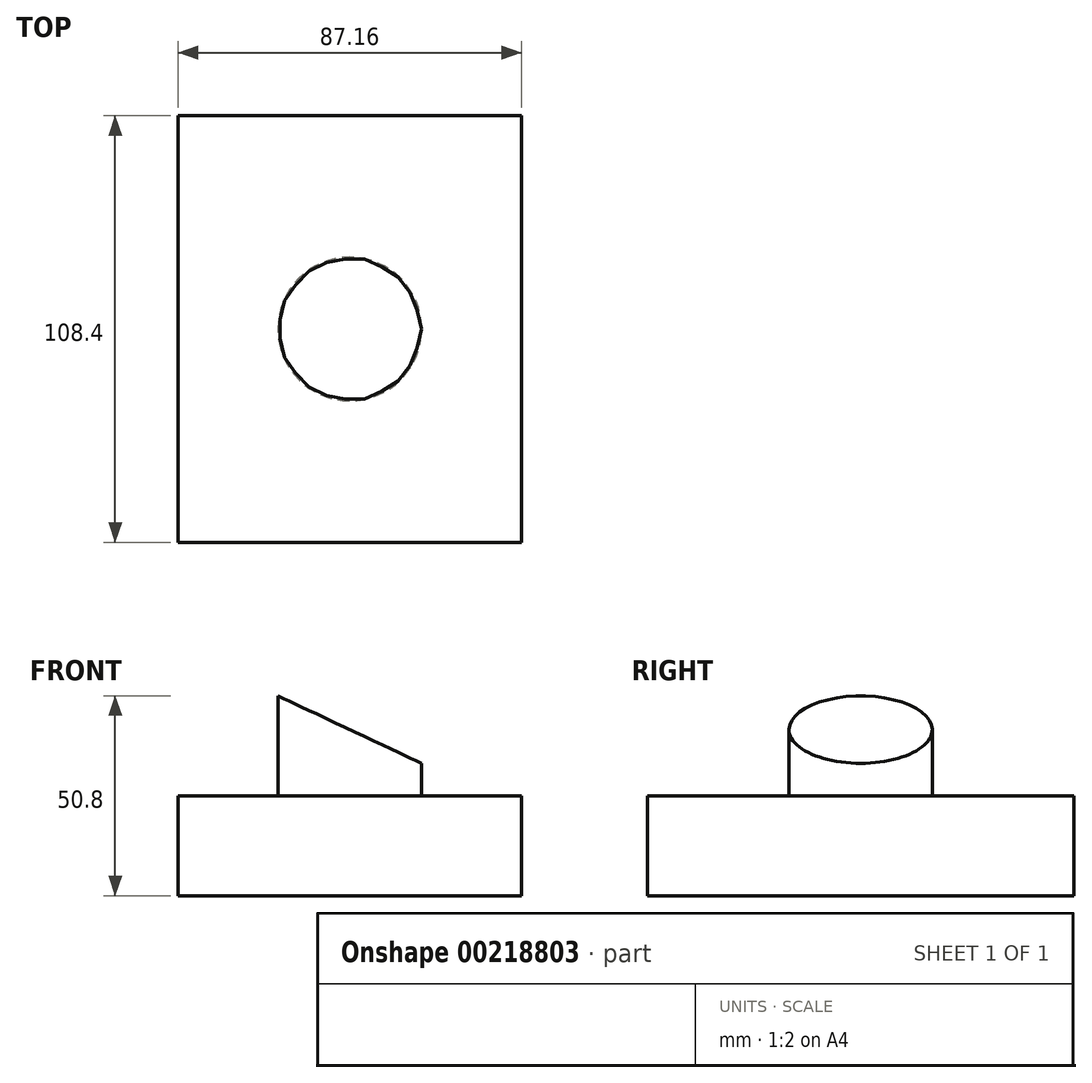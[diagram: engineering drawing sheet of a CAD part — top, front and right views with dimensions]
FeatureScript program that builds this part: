
annotation { "Feature Type Name" : "Feature", "Feature Type Description" : "" }
export const myFeature = defineFeature(function(context is Context, id is Id, definition is map)
    precondition{}
    {
        {
            var Q0;
            Q0=qCreatedBy(makeId("Top.planeOp"),FACE);
            var sketch = newSketch(context, id + "F0", { "sketchPlane" : qUnion([Q0])});
            skLineSegment(sketch, "E0.bottom", {"start": v(43.58, 54.2) * mm, "end": v(-43.58, 54.2) * mm});
            skLineSegment(sketch, "E0.top", {"start": v(43.58, -54.2) * mm, "end": v(-43.58, -54.2) * mm});
            skLineSegment(sketch, "E0.left", {"start": v(43.58, 54.2) * mm, "end": v(43.58, -54.2) * mm});
            skLineSegment(sketch, "E0.right", {"start": v(-43.58, 54.2) * mm, "end": v(-43.58, -54.2) * mm});
            skPoint(sketch, "E0.middle", {"position": v(0, 0) * mm});
            skSolve(sketch);
        }
        {
            var Q0;
            Q0=makeQuery(id+"F0.imprint","IMPRINT",FACE,{"disambiguationData":[TD([[makeQuery(id+"F0.imprint","IMPRINT",EDGE,{"derivedFrom":sQuery(id+"F0.wireOp",EDGE,"E0.bottom")}),1.0]])]});
            extrude(context, id + "F1", {"entities" : qUnion([Q0]), "depth" : 25.4 * mm});
        }
        {
            var Q0;
            Q0=makeQuery(id+"F1.opExtrude","CAP_FACE",FACE,{"disambiguationData":[OSD([sQuery(id+"F0.wireOp",EDGE,"E0.bottom"),sQuery(id+"F0.wireOp",EDGE,"E0.top"),sQuery(id+"F0.wireOp",EDGE,"E0.left"),sQuery(id+"F0.wireOp",EDGE,"E0.right")])],"isStart":false});
            var sketch = newSketch(context, id + "F2", { "sketchPlane" : qUnion([Q0])});
            skCircle(sketch, "E1", {"center": v(0, 0) * mm, "radius": 18.23 * mm});
            skSolve(sketch);
        }
        {
            var Q0;
            Q0=makeQuery(id+"F2.imprint","IMPRINT",FACE,{"disambiguationData":[TD([[makeQuery(id+"F2.imprint","IMPRINT",EDGE,{"derivedFrom":sQuery(id+"F2.wireOp",EDGE,"E1")}),1.0]])]});
            extrude(context, id + "F3", {"entities" : qUnion([Q0]), "operationType" : NewBodyOperationType.ADD, "depth" : 25.4 * mm});
        }
        {
            var Q0;
            Q0=qCreatedBy(makeId("Front.planeOp"),FACE);
            var sketch = newSketch(context, id + "F4", { "sketchPlane" : qUnion([Q0])});
            skLineSegment(sketch, "E2", {"start": v(-18.23, 25.4) * mm, "end": v(-18.23, 50.8) * mm});
            skLineSegment(sketch, "E3", {"start": v(18.23, 50.8) * mm, "end": v(18.23, 25.4) * mm});
            skLineSegment(sketch, "E4.0", {"start": v(-18.23, 50.8) * mm, "end": v(18.23, 50.8) * mm});
            skLineSegment(sketch, "E5", {"start": v(-18.23, 50.8) * mm, "end": v(18.23, 33.66) * mm});
            skLineSegment(sketch, "E6", {"start": v(18.23, 33.66) * mm, "end": v(18.23, 50.8) * mm});
            skSolve(sketch);
        }
        {
            var Q0;
            Q0 = qSketchRegion(id + "F4", true);
            extrude(context, id + "F5", {"entities" : qUnion([Q0]), "operationType" : NewBodyOperationType.REMOVE, "endBound" : BoundingType.SYMMETRIC, "oppositeDirection" : true, "depth" : 76.2 * mm});
        }
    });
